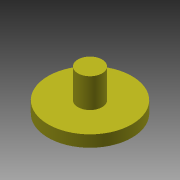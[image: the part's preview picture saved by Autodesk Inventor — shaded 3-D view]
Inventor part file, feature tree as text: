
AUTODESK INVENTOR PART (.ipt)
format: ipt  version: 2013 (Build 170138000, 138)  size: 75,776 bytes
history: native  units: mm
features: extrude x2, sketch x2, other x1
ambient origin geometry x8: Origin, YZ Plane, XZ Plane, XY Plane, X Axis, Y Axis, Z Axis, Center Point
feature tree (5):
  other  "ソリッド1"
  extrude  "押し出し1"  Depth=16.6mm
  extrude  "押し出し2"  Depth=2.3mm TaperAngle=0.0deg
  sketch  "スケッチ1"
  sketch  "スケッチ2"
